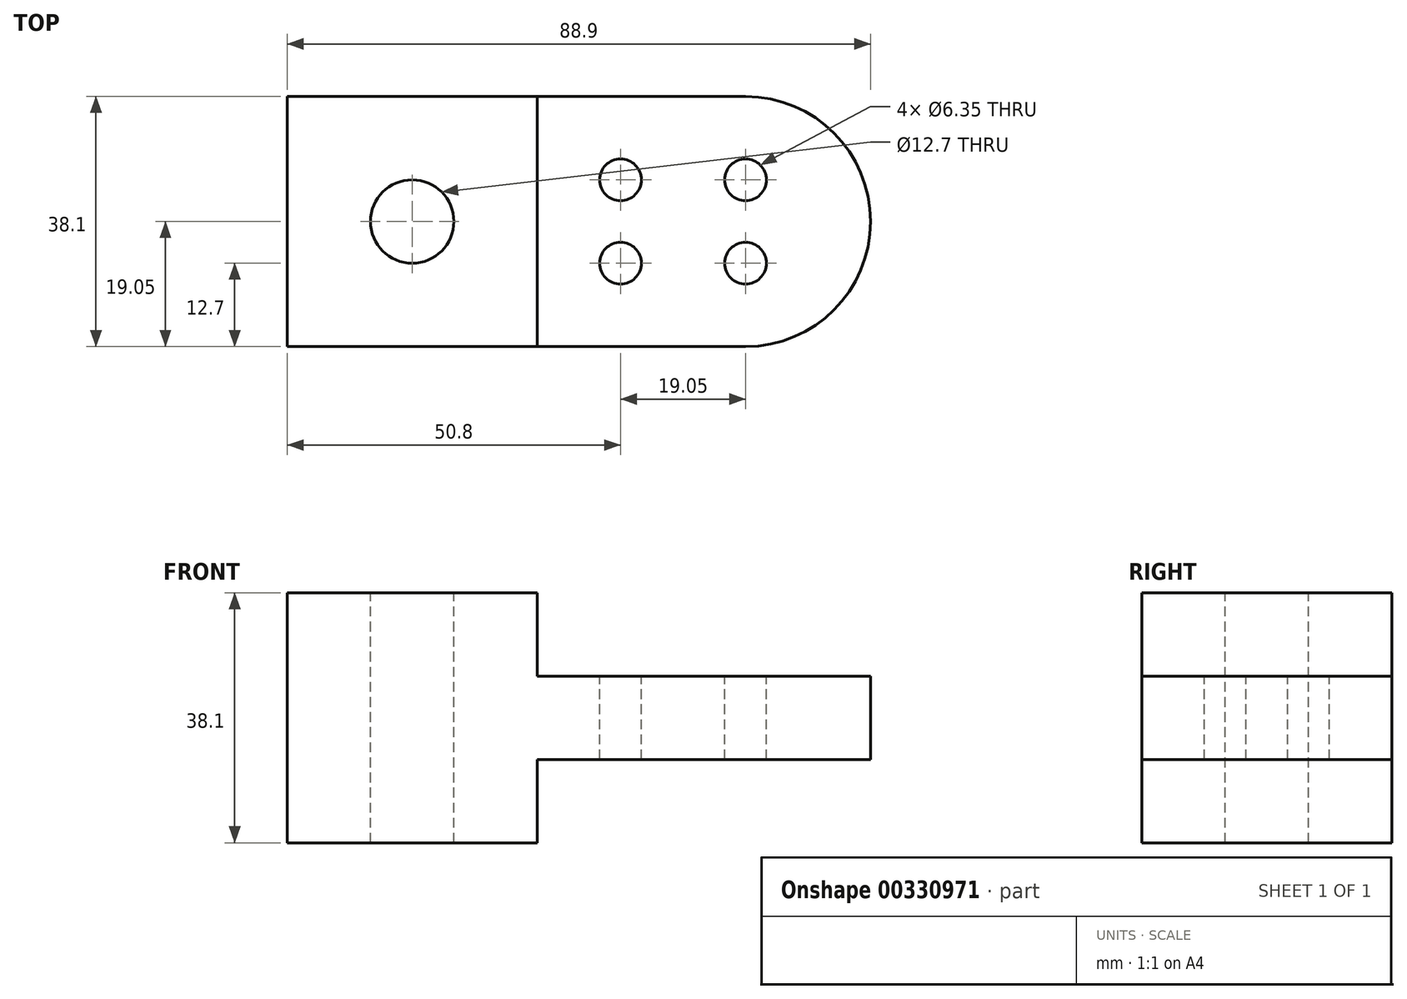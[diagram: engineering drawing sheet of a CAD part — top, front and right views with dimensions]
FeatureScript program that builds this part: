
annotation { "Feature Type Name" : "Feature", "Feature Type Description" : "" }
export const myFeature = defineFeature(function(context is Context, id is Id, definition is map)
    precondition{}
    {
        {
            var Q0;
            Q0=qCreatedBy(makeId("Front.planeOp"),FACE);
            var sketch = newSketch(context, id + "F0", { "sketchPlane" : qUnion([Q0])});
            skLineSegment(sketch, "E0.bottom", {"start": v(0, 0) * mm, "end": v(38.1, 0) * mm});
            skLineSegment(sketch, "E0.top", {"start": v(0, -38.1) * mm, "end": v(38.1, -38.1) * mm});
            skLineSegment(sketch, "E0.left", {"start": v(0, 0) * mm, "end": v(0, -38.1) * mm});
            skLineSegment(sketch, "E0.right", {"start": v(38.1, 0) * mm, "end": v(38.1, -12.7) * mm});
            skLineSegment(sketch, "E1", {"start": v(38.1, -12.7) * mm, "end": v(88.9, -12.7) * mm});
            skLineSegment(sketch, "E2", {"start": v(88.9, -12.7) * mm, "end": v(88.9, -25.4) * mm});
            skLineSegment(sketch, "E3", {"start": v(88.9, -25.4) * mm, "end": v(38.1, -25.4) * mm});
            skLineSegment(sketch, "E4.trimOffspring", {"start": v(38.1, -25.4) * mm, "end": v(38.1, -38.1) * mm});
            skSolve(sketch);
        }
        {
            var Q0;
            Q0=makeQuery(id+"F0.imprint","IMPRINT",FACE,{"disambiguationData":[TD([[makeQuery(id+"F0.imprint","IMPRINT",EDGE,{"derivedFrom":sQuery(id+"F0.wireOp",EDGE,"E0.bottom")}),-1.0]])]});
            extrude(context, id + "F1", {"entities" : qUnion([Q0]), "oppositeDirection" : true, "depth" : 38.1 * mm});
        }
        {
            var Q0;
            Q0=makeQuery(id+"F1.opExtrude","SWEPT_FACE",FACE,{"disambiguationData":[OSD([sQuery(id+"F0.wireOp",EDGE,"E0.bottom")])]});
            var sketch = newSketch(context, id + "F2", { "sketchPlane" : qUnion([Q0])});
            skCircle(sketch, "E5", {"center": v(19.05, 19.05) * mm, "radius": 6.35 * mm});
            skCircle(sketch, "E6", {"center": v(50.8, 25.4) * mm, "radius": 3.18 * mm});
            skCircle(sketch, "E7", {"center": v(69.85, 25.4) * mm, "radius": 3.18 * mm});
            skCircle(sketch, "E8", {"center": v(50.8, 12.7) * mm, "radius": 3.18 * mm});
            skCircle(sketch, "E9", {"center": v(69.85, 12.7) * mm, "radius": 3.18 * mm});
            skCircle(sketch, "E10", {"center": v(69.85, 19.05) * mm, "radius": 19.05 * mm});
            skLineSegment(sketch, "E11", {"start": v(56.45, 38.1) * mm, "end": v(88.9, 38.1) * mm});
            skLineSegment(sketch, "E12", {"start": v(88.9, 38.1) * mm, "end": v(88.9, 0) * mm});
            skLineSegment(sketch, "E13", {"start": v(88.9, 0) * mm, "end": v(60.84, 0) * mm});
            skSolve(sketch);
        }
        {
            var Q0;
            Q0=makeQuery(id+"F2.imprint","IMPRINT",FACE,{"disambiguationData":[TD([[makeQuery(id+"F2.imprint","IMPRINT",EDGE,{"derivedFrom":sQuery(id+"F2.wireOp",EDGE,"E5")}),1.0]])]});
            var Q1;
            {var subQ0=sQuery(id+"F2.wireOp",EDGE,"E10");var subQ1=sQuery(id+"F2.wireOp",EDGE,"E6");var subQ2=makeQuery(id+"F2.imprint","INTERSECT",VERTEX,{"disambiguationData":[OD(0.0)],"derivedFrom":[subQ1,subQ0]});Q1=makeQuery(id+"F2.imprint","IMPRINT",FACE,{"disambiguationData":[TD([[makeQuery(id+"F2.imprint","IMPRINT",EDGE,{"disambiguationData":[TD([[subQ2,-1.0]])],"derivedFrom":subQ1}),1.0]])]});}
            var Q2;
            {var subQ0=sQuery(id+"F2.wireOp",EDGE,"E10");var subQ1=sQuery(id+"F2.wireOp",EDGE,"E8");var subQ2=makeQuery(id+"F2.imprint","INTERSECT",VERTEX,{"disambiguationData":[OD(0.0)],"derivedFrom":[subQ1,subQ0]});Q2=makeQuery(id+"F2.imprint","IMPRINT",FACE,{"disambiguationData":[TD([[makeQuery(id+"F2.imprint","IMPRINT",EDGE,{"disambiguationData":[TD([[subQ2,-1.0]])],"derivedFrom":subQ1}),1.0]])]});}
            var Q3;
            {var subQ0=sQuery(id+"F2.wireOp",EDGE,"E11");var subQ1=sQuery(id+"F2.wireOp",EDGE,"E10");var subQ2=makeQuery(id+"F2.imprint","INTERSECT",VERTEX,{"derivedFrom":[subQ1,subQ0]});Q3=makeQuery(id+"F2.imprint","IMPRINT",FACE,{"disambiguationData":[TD([[makeQuery(id+"F2.imprint","IMPRINT",EDGE,{"disambiguationData":[TD([[subQ2,1.0]])],"derivedFrom":subQ1}),-1.0]])]});}
            var Q4;
            {var subQ0=sQuery(id+"F2.wireOp",EDGE,"E13");var subQ1=sQuery(id+"F2.wireOp",EDGE,"E10");var subQ2=makeQuery(id+"F2.imprint","INTERSECT",VERTEX,{"derivedFrom":[subQ1,subQ0]});Q4=makeQuery(id+"F2.imprint","IMPRINT",FACE,{"disambiguationData":[TD([[makeQuery(id+"F2.imprint","IMPRINT",EDGE,{"disambiguationData":[TD([[subQ2,-1.0]])],"derivedFrom":subQ1}),-1.0]])]});}
            var Q5;
            {var subQ0=sQuery(id+"F2.wireOp",EDGE,"E10");var subQ1=sQuery(id+"F2.wireOp",EDGE,"E6");var subQ2=makeQuery(id+"F2.imprint","INTERSECT",VERTEX,{"disambiguationData":[OD(0.0)],"derivedFrom":[subQ1,subQ0]});Q5=makeQuery(id+"F2.imprint","IMPRINT",FACE,{"disambiguationData":[TD([[makeQuery(id+"F2.imprint","IMPRINT",EDGE,{"disambiguationData":[TD([[subQ2,1.0]])],"derivedFrom":subQ1}),1.0]])]});}
            var Q6;
            {var subQ0=sQuery(id+"F2.wireOp",EDGE,"E10");var subQ1=sQuery(id+"F2.wireOp",EDGE,"E8");var subQ2=makeQuery(id+"F2.imprint","INTERSECT",VERTEX,{"disambiguationData":[OD(0.0)],"derivedFrom":[subQ1,subQ0]});Q6=makeQuery(id+"F2.imprint","IMPRINT",FACE,{"disambiguationData":[TD([[makeQuery(id+"F2.imprint","IMPRINT",EDGE,{"disambiguationData":[TD([[subQ2,1.0]])],"derivedFrom":subQ1}),1.0]])]});}
            var Q7;
            Q7=makeQuery(id+"F2.imprint","IMPRINT",FACE,{"disambiguationData":[TD([[makeQuery(id+"F2.imprint","IMPRINT",EDGE,{"derivedFrom":sQuery(id+"F2.wireOp",EDGE,"E9")}),1.0]])]});
            var Q8;
            Q8=makeQuery(id+"F2.imprint","IMPRINT",FACE,{"disambiguationData":[TD([[makeQuery(id+"F2.imprint","IMPRINT",EDGE,{"derivedFrom":sQuery(id+"F2.wireOp",EDGE,"E7")}),1.0]])]});
            extrude(context, id + "F3", {"entities" : qUnion([Q0, Q1, Q2, Q3, Q4, Q5, Q6, Q7, Q8]), "operationType" : NewBodyOperationType.REMOVE, "endBound" : BoundingType.THROUGH_ALL, "oppositeDirection" : true, "depth" : 25.4 * mm});
        }
    });
